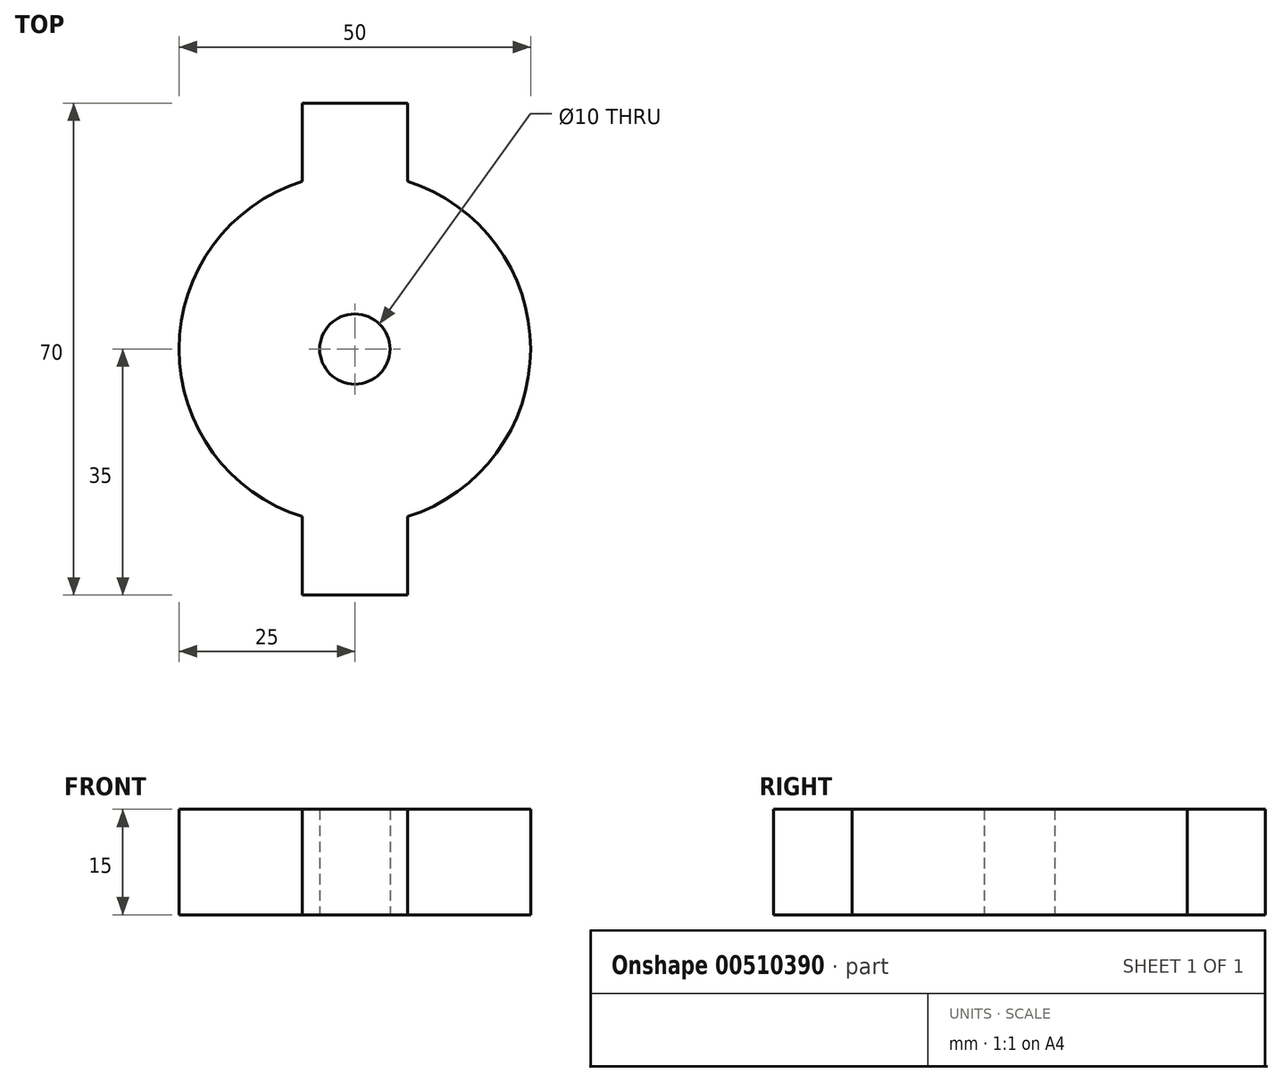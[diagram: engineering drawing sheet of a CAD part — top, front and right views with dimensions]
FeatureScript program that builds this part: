
annotation { "Feature Type Name" : "Feature", "Feature Type Description" : "" }
export const myFeature = defineFeature(function(context is Context, id is Id, definition is map)
    precondition{}
    {
        {
            var Q0;
            Q0=qCreatedBy(makeId("Top.planeOp"),FACE);
            var sketch = newSketch(context, id + "F0", { "sketchPlane" : qUnion([Q0])});
            skCircle(sketch, "E0", {"center": v(0, 0) * mm, "radius": 25 * mm});
            skCircle(sketch, "E1", {"center": v(0, 0) * mm, "radius": 5 * mm});
            skLineSegment(sketch, "E2.bottom", {"start": v(7.5, 35) * mm, "end": v(-7.5, 35) * mm});
            skLineSegment(sketch, "E2.top", {"start": v(7.5, -35) * mm, "end": v(-7.5, -35) * mm});
            skLineSegment(sketch, "E2.left", {"start": v(7.5, 35) * mm, "end": v(7.5, 23.85) * mm});
            skLineSegment(sketch, "E2.right", {"start": v(-7.5, 35) * mm, "end": v(-7.5, 23.85) * mm});
            skLineSegment(sketch, "E3.trimOffspring", {"start": v(-7.5, -23.85) * mm, "end": v(-7.5, -35) * mm});
            skLineSegment(sketch, "E4.trimOffspring", {"start": v(7.5, -23.85) * mm, "end": v(7.5, -35) * mm});
            skSolve(sketch);
        }
        {
            var Q0;
            Q0=makeQuery(id+"F0.imprint","IMPRINT",FACE,{"disambiguationData":[TD([[makeQuery(id+"F0.imprint","IMPRINT",EDGE,{"derivedFrom":sQuery(id+"F0.wireOp",EDGE,"E0")}),1.0]])]});
            var Q1;
            Q1=makeQuery(id+"F0.imprint","IMPRINT",FACE,{"disambiguationData":[TD([[makeQuery(id+"F0.imprint","IMPRINT",EDGE,{"derivedFrom":sQuery(id+"F0.wireOp",EDGE,"E2.bottom")}),1.0]])]});
            var Q2;
            Q2=makeQuery(id+"F0.imprint","IMPRINT",FACE,{"disambiguationData":[TD([[makeQuery(id+"F0.imprint","IMPRINT",EDGE,{"derivedFrom":sQuery(id+"F0.wireOp",EDGE,"E2.top")}),-1.0]])]});
            extrude(context, id + "F1", {"entities" : qUnion([Q0, Q1, Q2]), "endBound" : BoundingType.SYMMETRIC, "depth" : 15 * mm});
        }
    });
